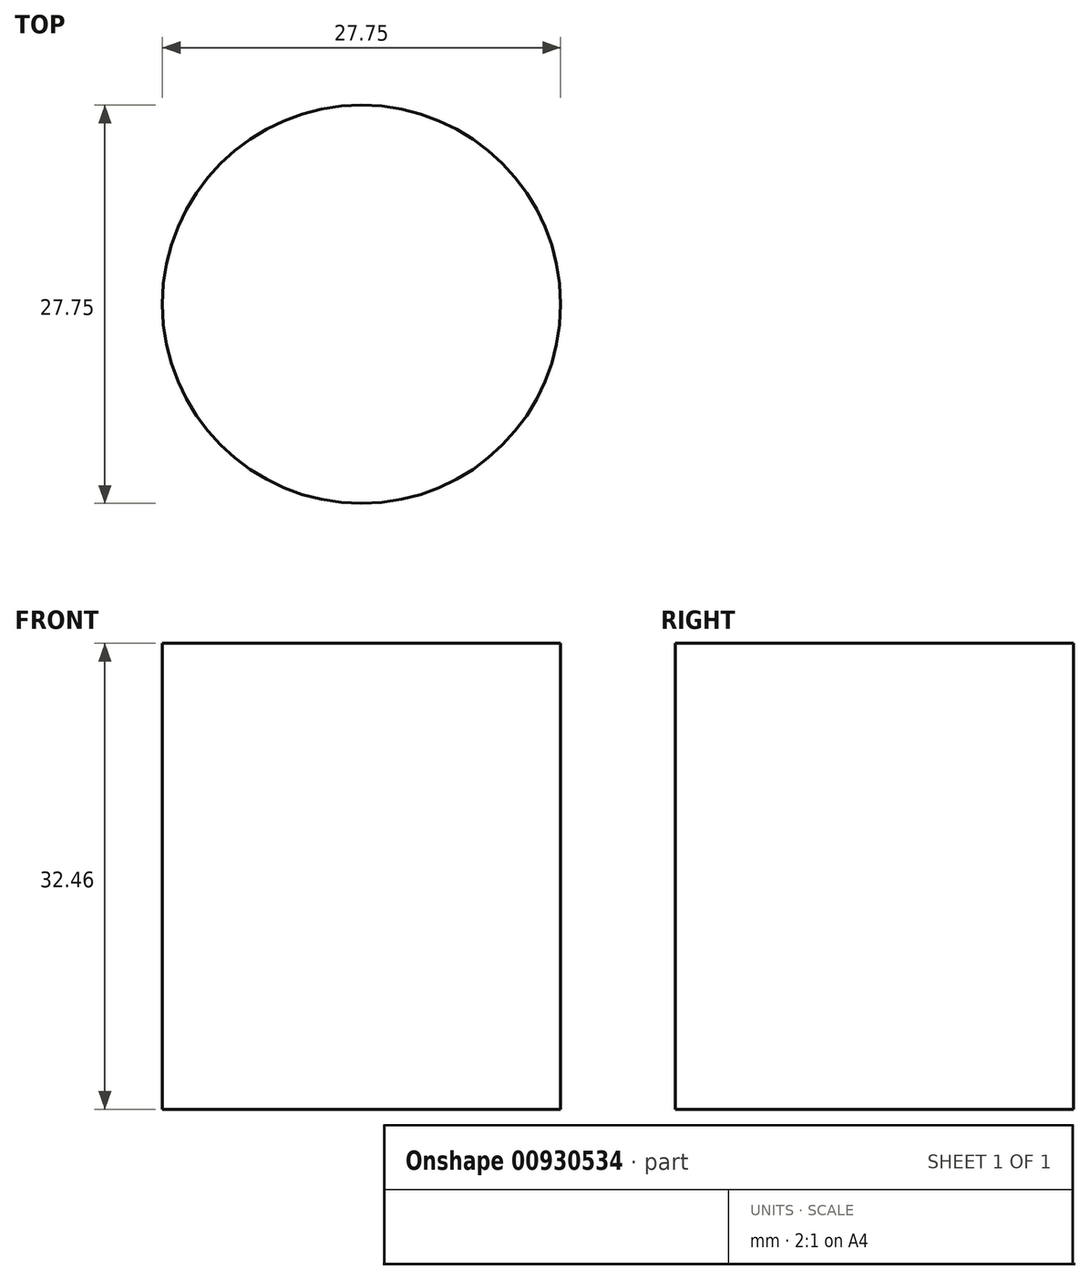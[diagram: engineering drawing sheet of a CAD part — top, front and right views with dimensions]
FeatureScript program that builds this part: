
annotation { "Feature Type Name" : "Feature", "Feature Type Description" : "" }
export const myFeature = defineFeature(function(context is Context, id is Id, definition is map)
    precondition{}
    {
        {
            var Q0;
            Q0=qCreatedBy(makeId("Top.planeOp"),FACE);
            var sketch = newSketch(context, id + "F0", { "sketchPlane" : qUnion([Q0])});
            skCircle(sketch, "E0", {"center": v(6.79, -3.48) * mm, "radius": 13.88 * mm});
            skSolve(sketch);
        }
        {
            var Q0;
            Q0=sQuery(id+"F0.wireOp",EDGE,"E0");
            extrude(context, id + "F1", {"bodyType" : ToolBodyType.SURFACE, "surfaceEntities" : qUnion([Q0]), "depth" : 32.46 * mm, "offsetDistance" : 25.4 * mm});
        }
    });
